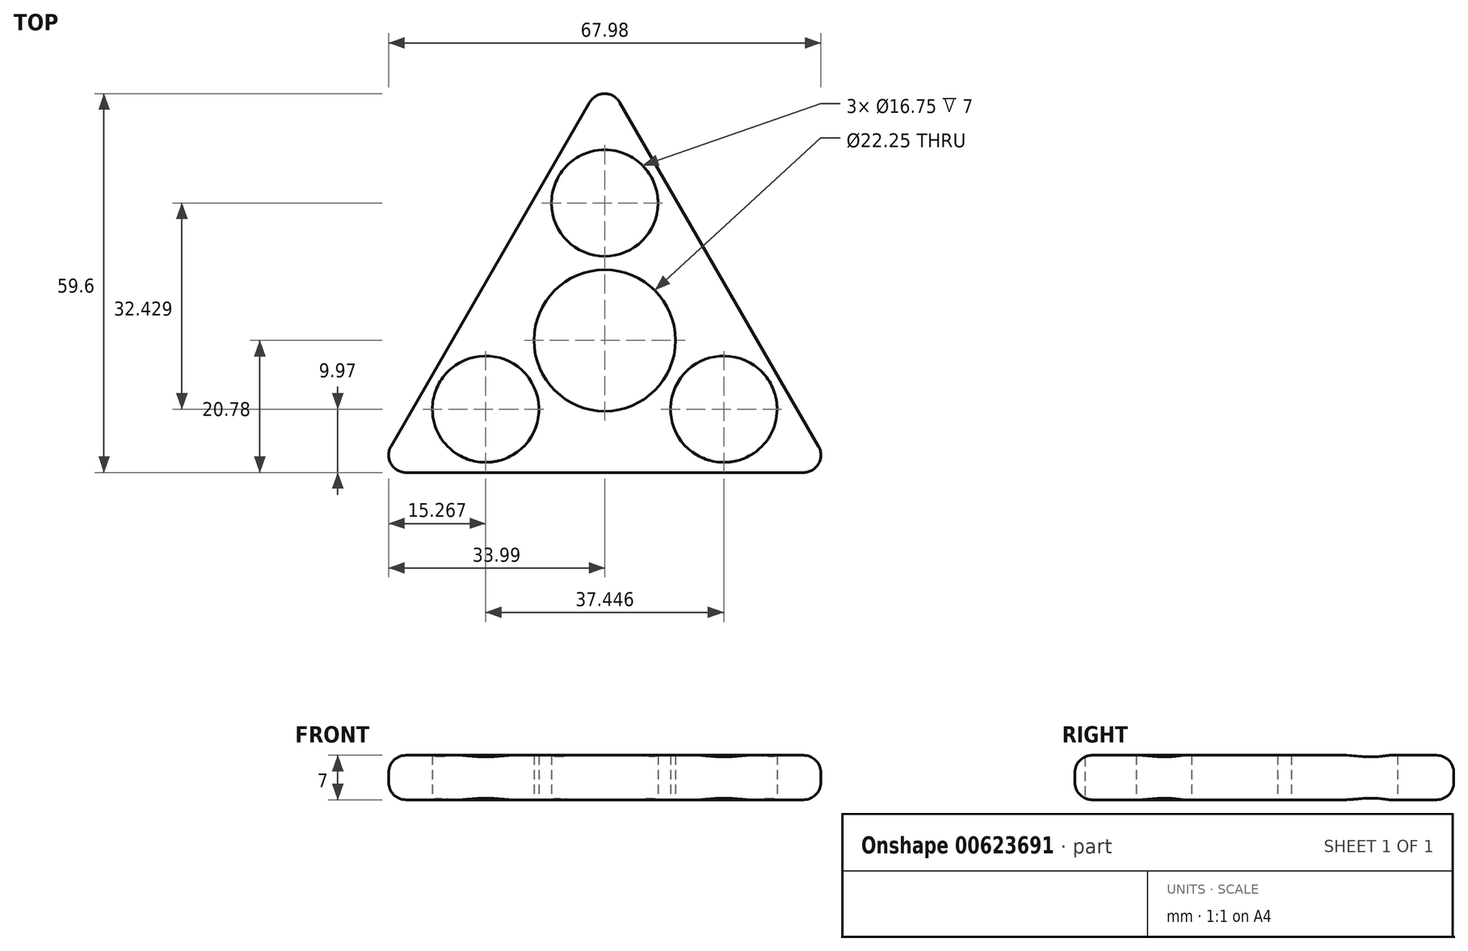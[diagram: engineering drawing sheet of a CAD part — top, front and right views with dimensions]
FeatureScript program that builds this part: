
annotation { "Feature Type Name" : "Feature", "Feature Type Description" : "" }
export const myFeature = defineFeature(function(context is Context, id is Id, definition is map)
    precondition{}
    {
        {
            var Q0;
            Q0=qCreatedBy(makeId("Top.planeOp"),FACE);
            var sketch = newSketch(context, id + "F0", { "sketchPlane" : qUnion([Q0])});
            skCircle(sketch, "E0", {"center": v(0, 0) * mm, "radius": 11.12 * mm});
            skCircle(sketch, "E1.cCircle", {"center": v(0, 0) * mm, "radius": 20.78 * mm, "construction": true});
            skLineSegment(sketch, "E1.0", {"start": v(0, 41.57) * mm, "end": v(36, -20.78) * mm});
            skLineSegment(sketch, "E1.1", {"start": v(36, -20.78) * mm, "end": v(-36, -20.78) * mm});
            skLineSegment(sketch, "E1.2", {"start": v(-36, -20.78) * mm, "end": v(0, 41.57) * mm});
            skPoint(sketch, "E1.0.midPoint", {"position": v(18, 10.4) * mm});
            skCircle(sketch, "E2", {"center": v(0, 21.62) * mm, "radius": 8.38 * mm});
            skPoint(sketch, "E3", {"position": v(-18, 10.4) * mm});
            skCircle(sketch, "E4", {"center": v(-18.72, -10.8) * mm, "radius": 8.38 * mm});
            skCircle(sketch, "E5", {"center": v(18.72, -10.8) * mm, "radius": 8.38 * mm});
            skSolve(sketch);
        }
        {
            var Q0;
            Q0=makeQuery(id+"F0.imprint","IMPRINT",FACE,{"disambiguationData":[TD([[makeQuery(id+"F0.imprint","IMPRINT",EDGE,{"derivedFrom":sQuery(id+"F0.wireOp",EDGE,"E0")}),-1.0]])]});
            extrude(context, id + "F1", {"entities" : qUnion([Q0]), "depth" : 7 * mm, "offsetDistance" : 25 * mm});
        }
        {
            var Q0;
            Q0=makeQuery(id+"F1.opExtrude","SWEPT_FACE",FACE,{"disambiguationData":[OSD([sQuery(id+"F0.wireOp",EDGE,"E1.1")])]});
            var Q1;
            Q1=makeQuery(id+"F1.opExtrude","SWEPT_FACE",FACE,{"disambiguationData":[OSD([sQuery(id+"F0.wireOp",EDGE,"E1.0")])]});
            var Q2;
            Q2=qNothing();
            var Q3;
            Q3=makeQuery(id+"F1.opExtrude","SWEPT_FACE",FACE,{"disambiguationData":[OSD([sQuery(id+"F0.wireOp",EDGE,"E1.2")])]});
            fillet(context, id + "F2", {"entities" : qUnion([Q0, Q1, Q2, Q3]), "radius" : 2.75 * mm, "tangentPropagation" : true, "allowEdgeOverflow" : false});
        }
    });
